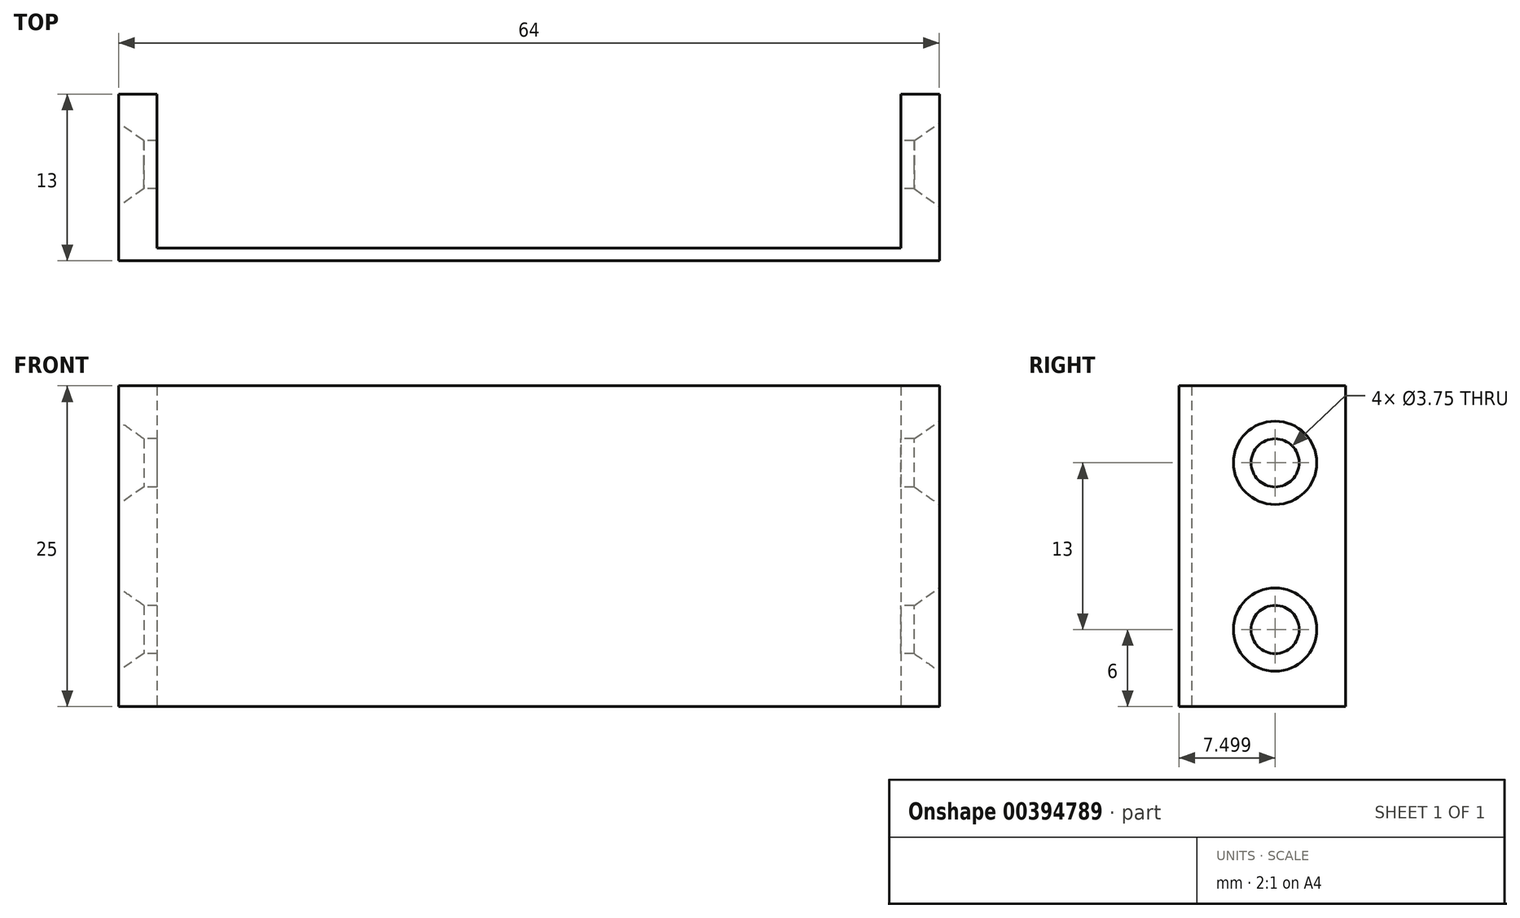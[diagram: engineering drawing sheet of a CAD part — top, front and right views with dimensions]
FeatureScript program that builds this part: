
annotation { "Feature Type Name" : "Feature", "Feature Type Description" : "" }
export const myFeature = defineFeature(function(context is Context, id is Id, definition is map)
    precondition{}
    {
        {
            var Q0;
            Q0=qCreatedBy(makeId("Top.planeOp"),FACE);
            var sketch = newSketch(context, id + "F0", { "sketchPlane" : qUnion([Q0])});
            skLineSegment(sketch, "E0", {"start": v(-26.2, 6.95) * mm, "end": v(-26.2, -6.05) * mm});
            skLineSegment(sketch, "E1", {"start": v(-26.2, -6.05) * mm, "end": v(37.8, -6.05) * mm});
            skLineSegment(sketch, "E2", {"start": v(37.8, -6.05) * mm, "end": v(37.8, 6.95) * mm});
            skLineSegment(sketch, "E3", {"start": v(37.8, 6.95) * mm, "end": v(34.8, 6.95) * mm});
            skLineSegment(sketch, "E4", {"start": v(34.8, 6.95) * mm, "end": v(34.8, -5.05) * mm});
            skLineSegment(sketch, "E5", {"start": v(34.8, -5.05) * mm, "end": v(-23.2, -5.05) * mm});
            skLineSegment(sketch, "E6", {"start": v(-23.2, -5.05) * mm, "end": v(-23.2, 6.95) * mm});
            skLineSegment(sketch, "E7", {"start": v(-23.2, 6.95) * mm, "end": v(-26.2, 6.95) * mm});
            skSolve(sketch);
        }
        {
            var Q0;
            Q0=makeQuery(id+"F0.imprint","IMPRINT",FACE,{"disambiguationData":[TD([[makeQuery(id+"F0.imprint","IMPRINT",EDGE,{"derivedFrom":sQuery(id+"F0.wireOp",EDGE,"E0")}),1.0]])]});
            extrude(context, id + "F1", {"entities" : qUnion([Q0]), "depth" : 25 * mm});
        }
        {
            var Q0;
            Q0=makeQuery(id+"F1.opExtrude","SWEPT_FACE",FACE,{"disambiguationData":[OSD([sQuery(id+"F0.wireOp",EDGE,"E2")])]});
            var sketch = newSketch(context, id + "F2", { "sketchPlane" : qUnion([Q0])});
            skCircle(sketch, "E8", {"center": v(1.45, 19) * mm, "radius": 1.88 * mm});
            skCircle(sketch, "E9", {"center": v(1.45, 6) * mm, "radius": 1.88 * mm});
            skCircle(sketch, "E10", {"center": v(1.45, 19) * mm, "radius": 3.25 * mm});
            skCircle(sketch, "E11", {"center": v(1.45, 6) * mm, "radius": 3.25 * mm});
            skSolve(sketch);
        }
        {
            var Q0;
            Q0=makeQuery(id+"F1.opExtrude","SWEPT_FACE",FACE,{"disambiguationData":[OSD([sQuery(id+"F0.wireOp",EDGE,"E0")])]});
            var sketch = newSketch(context, id + "F3", { "sketchPlane" : qUnion([Q0])});
            skPoint(sketch, "E12", {"position": v(-1.45, 6) * mm});
            skPoint(sketch, "E13", {"position": v(-1.45, 19) * mm});
            skSolve(sketch);
        }
        {
            var Q0;
            Q0=sQuery(id+"F3.wireOp",VERTEX,"E12");
            var Q1;
            Q1=sQuery(id+"F3.wireOp",VERTEX,"E13");
            var Q2;
            Q2=makeQuery(id+"F1.opExtrude","SWEPT_BODY",BODY,{"disambiguationData":[OSD([sQuery(id+"F0.wireOp",EDGE,"E0"),sQuery(id+"F0.wireOp",EDGE,"E1"),sQuery(id+"F0.wireOp",EDGE,"E2"),sQuery(id+"F0.wireOp",EDGE,"E3"),sQuery(id+"F0.wireOp",EDGE,"E4"),sQuery(id+"F0.wireOp",EDGE,"E5"),sQuery(id+"F0.wireOp",EDGE,"E6"),sQuery(id+"F0.wireOp",EDGE,"E7")])]});
            hole(context, id + "F4", {"style" : HoleStyle.C_SINK, "endStyle" : HoleEndStyle.THROUGH, "holeDiameter" : 3.75 * mm, "cSinkDiameter" : 6.5 * mm, "cSinkAngle" : 70 * degree, "tappedDepth" : 12 * mm, "tapClearance" : 3, "startFromSketch" : true, "locations" : qUnion([Q0, Q1]), "scope" : qUnion([Q2])});
        }
        {
            var Q0;
            Q0=sQuery(id+"F2.wireOp",VERTEX,"E8.center");
            var Q1;
            Q1=sQuery(id+"F2.wireOp",VERTEX,"E9.center");
            var Q2;
            Q2=makeQuery(id+"F1.opExtrude","SWEPT_BODY",BODY,{"disambiguationData":[OSD([sQuery(id+"F0.wireOp",EDGE,"E0"),sQuery(id+"F0.wireOp",EDGE,"E1"),sQuery(id+"F0.wireOp",EDGE,"E2"),sQuery(id+"F0.wireOp",EDGE,"E3"),sQuery(id+"F0.wireOp",EDGE,"E4"),sQuery(id+"F0.wireOp",EDGE,"E5"),sQuery(id+"F0.wireOp",EDGE,"E6"),sQuery(id+"F0.wireOp",EDGE,"E7")])]});
            hole(context, id + "F5", {"style" : HoleStyle.C_SINK, "endStyle" : HoleEndStyle.THROUGH, "holeDiameter" : 3.75 * mm, "cSinkDiameter" : 6.5 * mm, "cSinkAngle" : 70 * degree, "tappedDepth" : 12 * mm, "tapClearance" : 3, "startFromSketch" : true, "locations" : qUnion([Q0, Q1]), "scope" : qUnion([Q2])});
        }
    });
